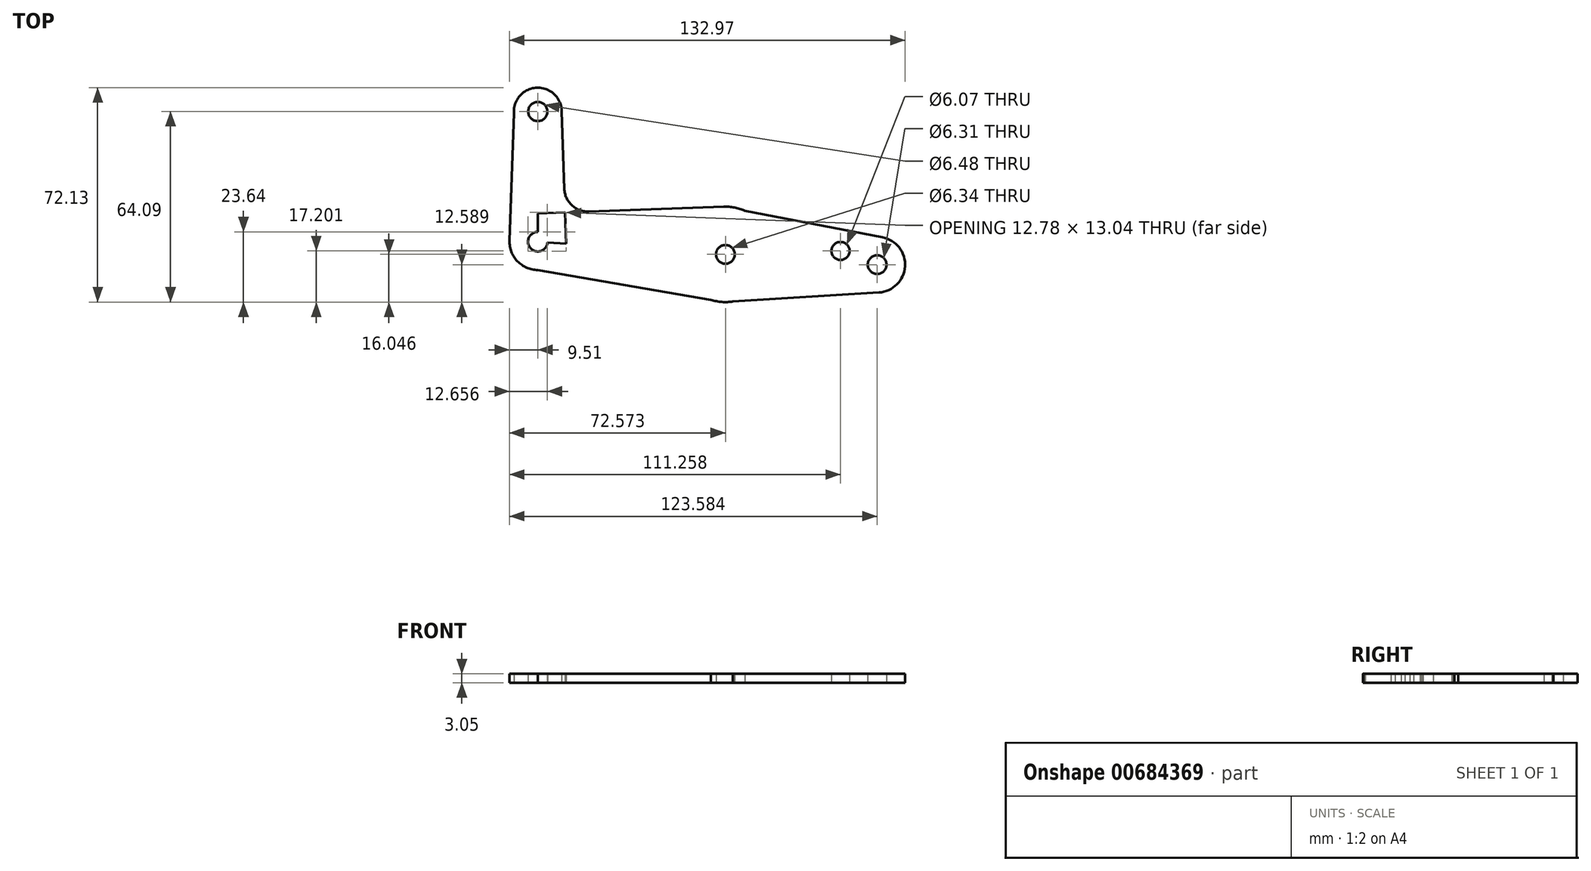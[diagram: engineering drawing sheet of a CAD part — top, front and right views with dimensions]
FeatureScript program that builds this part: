
annotation { "Feature Type Name" : "Feature", "Feature Type Description" : "" }
export const myFeature = defineFeature(function(context is Context, id is Id, definition is map)
    precondition{}
    {
        {
            var Q0;
            Q0=qCreatedBy(makeId("Top.planeOp"),FACE);
            var sketch = newSketch(context, id + "F0", { "sketchPlane" : qUnion([Q0])});
            skLineSegment(sketch, "E0", {"start": v(0, 0) * mm, "end": v(114.07, -7.73) * mm});
            skLineSegment(sketch, "E1", {"start": v(0, 0) * mm, "end": v(63.06, -4.27) * mm});
            skLineSegment(sketch, "E2", {"start": v(0, 0) * mm, "end": v(0, 43.77) * mm});
            skLineSegment(sketch, "E3", {"start": v(0, 43.77) * mm, "end": v(0, 0) * mm});
            skCircle(sketch, "E4", {"center": v(114.07, -7.73) * mm, "radius": 9.39 * mm});
            skCircle(sketch, "E5", {"center": v(63.06, -4.27) * mm, "radius": 16.05 * mm});
            skCircle(sketch, "E6", {"center": v(0, 0) * mm, "radius": 9.5 * mm});
            skCircle(sketch, "E7", {"center": v(0, 43.77) * mm, "radius": 8.04 * mm});
            skLineSegment(sketch, "E8", {"start": v(-7.97, 44.82) * mm, "end": v(-9.51, 0) * mm});
            skLineSegment(sketch, "E9", {"start": v(-9.51, 0) * mm, "end": v(-7.97, 44.82) * mm});
            skLineSegment(sketch, "E10", {"start": v(8.04, 43.77) * mm, "end": v(9.54, -0.65) * mm});
            skLineSegment(sketch, "E11", {"start": v(8.91, 17.8) * mm, "end": v(8.04, 43.77) * mm});
            skLineSegment(sketch, "E12", {"start": v(0, -9.5) * mm, "end": v(62.5, -20.31) * mm});
            skLineSegment(sketch, "E13", {"start": v(62.5, -20.31) * mm, "end": v(0, -9.5) * mm});
            skLineSegment(sketch, "E14", {"start": v(0, 9.5) * mm, "end": v(62.5, 11.76) * mm});
            skLineSegment(sketch, "E15", {"start": v(62.5, 11.76) * mm, "end": v(17.15, 10.13) * mm});
            skLineSegment(sketch, "E16", {"start": v(62.5, 11.76) * mm, "end": v(115.85, 1.49) * mm});
            skLineSegment(sketch, "E17", {"start": v(115.85, 1.49) * mm, "end": v(62.5, 11.76) * mm});
            skLineSegment(sketch, "E18", {"start": v(62.5, -20.31) * mm, "end": v(115.85, -17.03) * mm});
            skLineSegment(sketch, "E19", {"start": v(115.85, -17.03) * mm, "end": v(62.5, -20.31) * mm});
            skCircle(sketch, "E20", {"center": v(0, 43.77) * mm, "radius": 3.24 * mm});
            skCircle(sketch, "E21", {"center": v(0, 0) * mm, "radius": 3.3 * mm});
            skCircle(sketch, "E22", {"center": v(63.06, -4.27) * mm, "radius": 3.17 * mm});
            skCircle(sketch, "E23", {"center": v(114.07, -7.73) * mm, "radius": 3.15 * mm});
            skCircle(sketch, "E24", {"center": v(101.75, -3.12) * mm, "radius": 3.03 * mm});
            skArc(sketch, "E25.filletArc", {"start": v(8.91, 17.8) * mm, "mid": v(11.44, 12.26) * mm, "end": v(17.15, 10.13) * mm});
            skSolve(sketch);
        }
        {
            var Q0;
            Q0 = qSketchRegion(id + "F0", true);
            var Q1;
            {var subQ0=sQuery(id+"F0.wireOp",EDGE,"E11");Q1=makeQuery(id+"F0.imprint","IMPRINT",FACE,{"disambiguationData":[TD([[makeQuery(id+"F0.imprint","IMPRINT",EDGE,{"derivedFrom":subQ0}),1.0]])]});}
            extrude(context, id + "F1", {"entities" : qUnion([Q0, Q1]), "depth" : 3.05 * mm, "offsetDistance" : 25.4 * mm});
        }
    });
